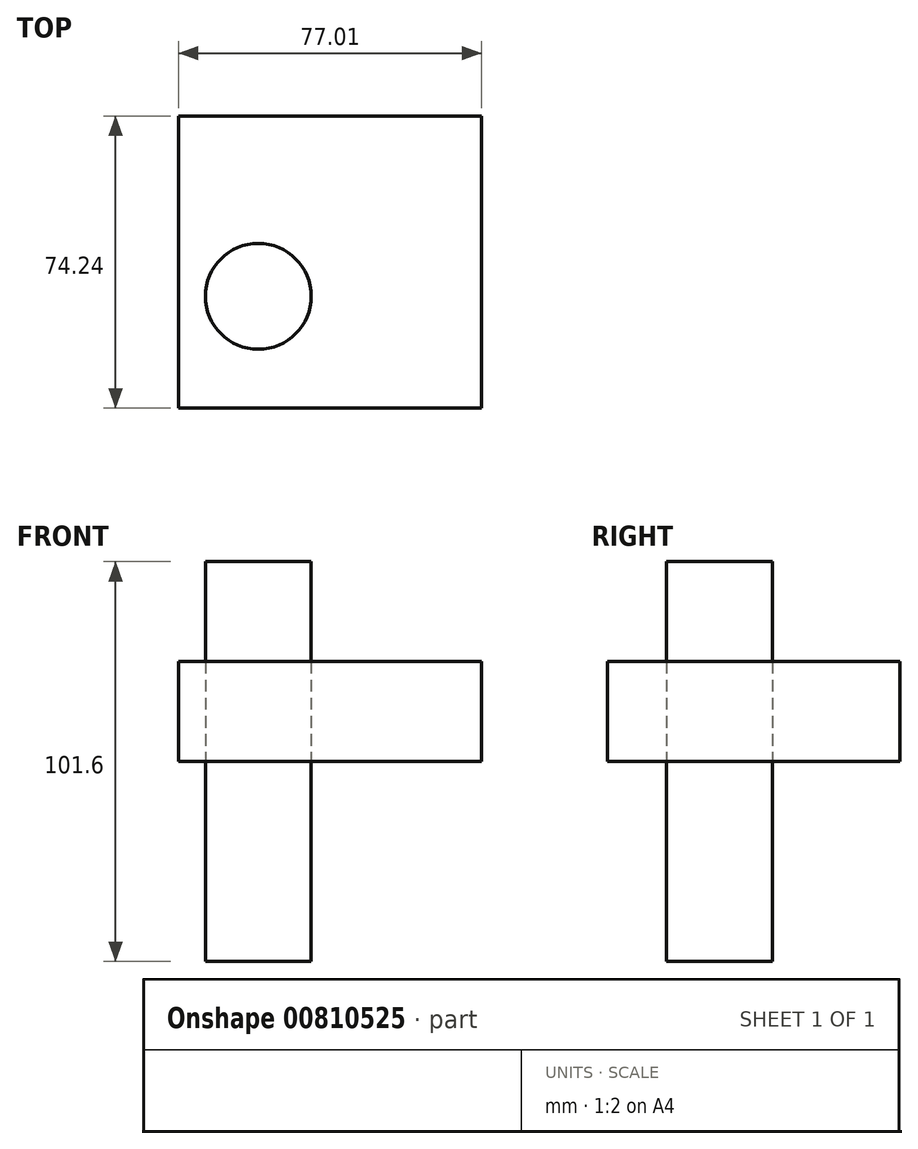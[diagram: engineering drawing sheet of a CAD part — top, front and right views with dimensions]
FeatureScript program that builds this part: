
annotation { "Feature Type Name" : "Feature", "Feature Type Description" : "" }
export const myFeature = defineFeature(function(context is Context, id is Id, definition is map)
    precondition{}
    {
        {
            var Q0;
            Q0=qCreatedBy(makeId("Top.planeOp"),FACE);
            var sketch = newSketch(context, id + "F0", { "sketchPlane" : qUnion([Q0])});
            skLineSegment(sketch, "E0.bottom", {"start": v(-67.54, -48.8) * mm, "end": v(9.47, -48.8) * mm});
            skLineSegment(sketch, "E0.top", {"start": v(-67.54, 25.44) * mm, "end": v(9.47, 25.44) * mm});
            skLineSegment(sketch, "E0.left", {"start": v(-67.54, -48.8) * mm, "end": v(-67.54, 25.44) * mm});
            skLineSegment(sketch, "E0.right", {"start": v(9.47, -48.8) * mm, "end": v(9.47, 25.44) * mm});
            skSolve(sketch);
        }
        {
            var Q0;
            Q0=qCreatedBy(makeId("Top.planeOp"),FACE);
            var sketch = newSketch(context, id + "F1", { "sketchPlane" : qUnion([Q0])});
            skCircle(sketch, "E1", {"center": v(-47.26, -20.38) * mm, "radius": 13.44 * mm});
            skSolve(sketch);
        }
        {
            var Q0;
            Q0=makeQuery(id+"F0.imprint","IMPRINT",FACE,{"disambiguationData":[TD([[makeQuery(id+"F0.imprint","IMPRINT",EDGE,{"derivedFrom":sQuery(id+"F0.wireOp",EDGE,"E0.bottom")}),1.0]])]});
            extrude(context, id + "F2", {"entities" : qUnion([Q0]), "depth" : 25.4 * mm, "offsetDistance" : 25.4 * mm});
        }
        {
            var Q0;
            Q0 = qSketchRegion(id + "F1", true);
            extrude(context, id + "F3", {"entities" : qUnion([Q0]), "depth" : 50.8 * mm, "offsetDistance" : 25.4 * mm, "hasSecondDirection" : true, "secondDirectionOppositeDirection" : true, "secondDirectionDepth" : 50.8 * mm});
        }
    });
